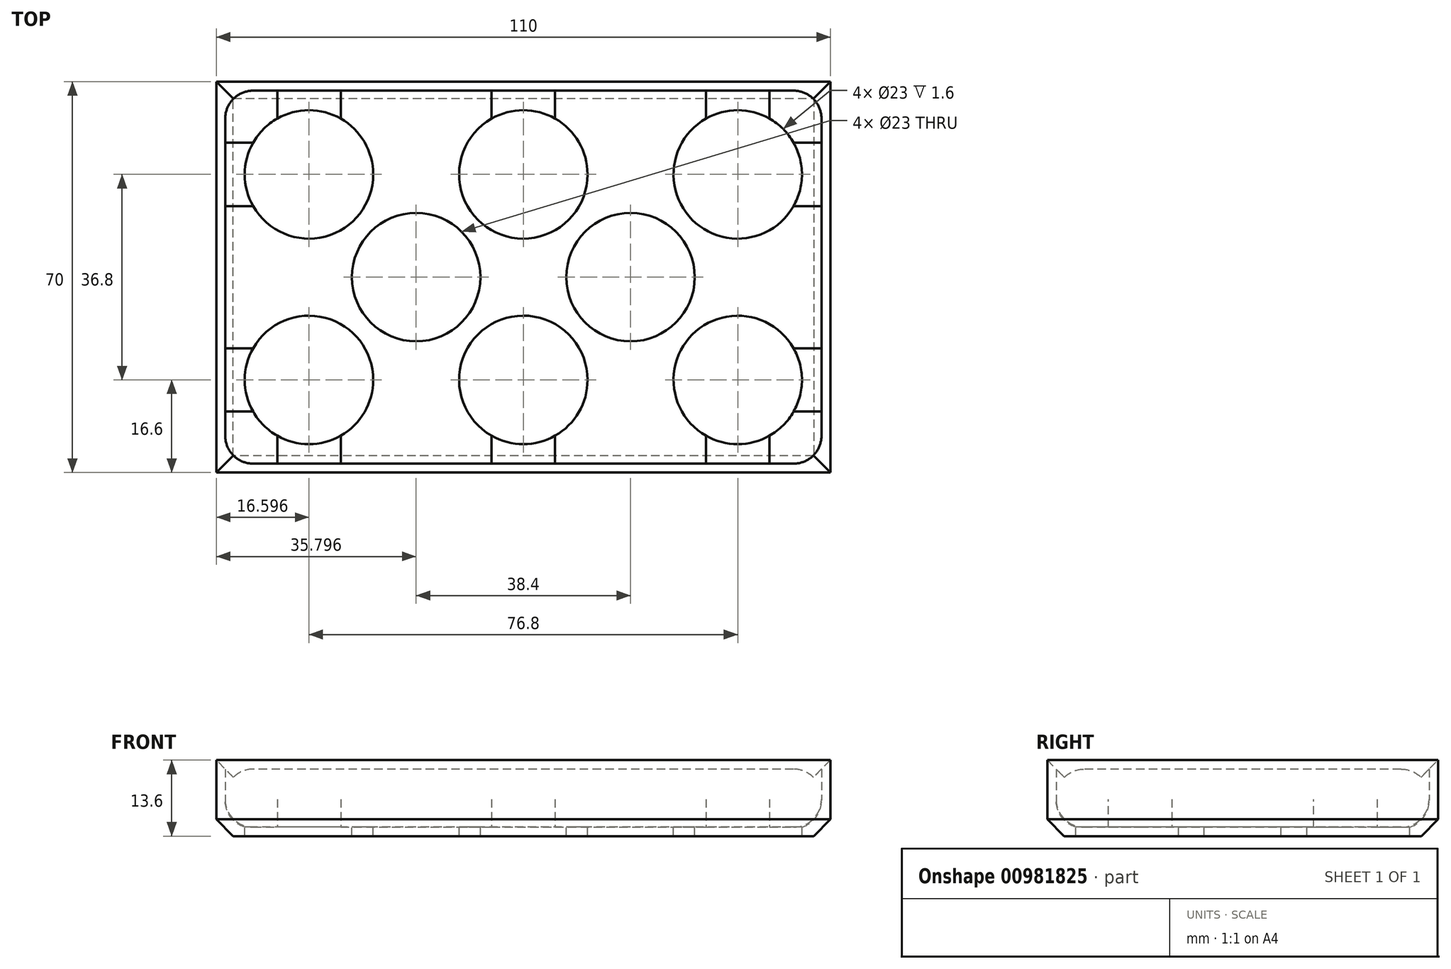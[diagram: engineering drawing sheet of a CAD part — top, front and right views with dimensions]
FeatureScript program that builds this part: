
annotation { "Feature Type Name" : "Feature", "Feature Type Description" : "" }
export const myFeature = defineFeature(function(context is Context, id is Id, definition is map)
    precondition{}
    {
        {
            var Q0;
            Q0=qCreatedBy(makeId("Top.planeOp"),FACE);
            var sketch = newSketch(context, id + "F0", { "sketchPlane" : qUnion([Q0])});
            skLineSegment(sketch, "E0.bottom", {"start": v(-42.8, 28.8) * mm, "end": v(67.2, 28.8) * mm});
            skLineSegment(sketch, "E0.top", {"start": v(-42.8, -41.2) * mm, "end": v(67.2, -41.2) * mm});
            skLineSegment(sketch, "E0.left", {"start": v(-42.8, 28.8) * mm, "end": v(-42.8, -41.2) * mm});
            skLineSegment(sketch, "E0.right", {"start": v(67.2, 28.8) * mm, "end": v(67.2, -41.2) * mm});
            skSolve(sketch);
        }
        {
            var Q0;
            Q0=makeQuery(id+"F0.imprint","IMPRINT",FACE,{"disambiguationData":[TD([[makeQuery(id+"F0.imprint","IMPRINT",EDGE,{"derivedFrom":sQuery(id+"F0.wireOp",EDGE,"E0.bottom")}),-1.0]])]});
            extrude(context, id + "F1", {"entities" : qUnion([Q0]), "depth" : 15 * mm, "offsetDistance" : 25 * mm});
        }
        {
            var Q0;
            Q0=makeQuery(id+"F1.opExtrude","CAP_FACE",FACE,{"disambiguationData":[OSD([sQuery(id+"F0.wireOp",EDGE,"E0.bottom"),sQuery(id+"F0.wireOp",EDGE,"E0.top"),sQuery(id+"F0.wireOp",EDGE,"E0.left"),sQuery(id+"F0.wireOp",EDGE,"E0.right")])],"isStart":false});
            shell(context, id + "F2", {"entities" : qUnion([Q0]), "thickness" : 1.6 * mm});
        }
        {
            var Q0;
            Q0=makeQuery(id+"F2.opShell","OFFSET_FACE",FACE,{"disambiguationData":[OSD([sQuery(id+"F0.wireOp",EDGE,"E0.bottom"),sQuery(id+"F0.wireOp",EDGE,"E0.top"),sQuery(id+"F0.wireOp",EDGE,"E0.left"),sQuery(id+"F0.wireOp",EDGE,"E0.right")])]});
            var sketch = newSketch(context, id + "F3", { "sketchPlane" : qUnion([Q0])});
            skCircle(sketch, "E1", {"center": v(50.6, 12.2) * mm, "radius": 11.5 * mm});
            skCircle(sketch, "E2.1.0.0", {"center": v(12.2, 12.2) * mm, "radius": 11.5 * mm});
            skCircle(sketch, "E2.2.0.0", {"center": v(-26.2, 12.2) * mm, "radius": 11.5 * mm});
            skLineSegment(sketch, "E2.direction1", {"start": v(50.6, 12.2) * mm, "end": v(12.2, 12.2) * mm, "construction": true});
            skCircle(sketch, "E3", {"center": v(50.6, -24.6) * mm, "radius": 11.5 * mm});
            skCircle(sketch, "E4.1.0.0", {"center": v(12.2, -24.6) * mm, "radius": 11.5 * mm});
            skCircle(sketch, "E4.2.0.0", {"center": v(-26.2, -24.6) * mm, "radius": 11.5 * mm});
            skLineSegment(sketch, "E4.direction1", {"start": v(50.6, -24.6) * mm, "end": v(12.2, -24.6) * mm, "construction": true});
            skCircle(sketch, "E5.2.0.0", {"center": v(-7, -6.2) * mm, "radius": 11.5 * mm});
            skCircle(sketch, "E6.1.0.0", {"center": v(31.4, -6.2) * mm, "radius": 11.5 * mm});
            skLineSegment(sketch, "E6.direction1", {"start": v(-7, -6.2) * mm, "end": v(31.4, -6.2) * mm, "construction": true});
            skSolve(sketch);
        }
        {
            var Q0;
            Q0=makeQuery(id+"F3.imprint","IMPRINT",FACE,{"disambiguationData":[TD([[makeQuery(id+"F3.imprint","IMPRINT",EDGE,{"derivedFrom":sQuery(id+"F3.wireOp",EDGE,"E2.3.0.0")}),1.0]])]});
            var Q1;
            Q1=makeQuery(id+"F3.imprint","IMPRINT",FACE,{"disambiguationData":[TD([[makeQuery(id+"F3.imprint","IMPRINT",EDGE,{"derivedFrom":sQuery(id+"F3.wireOp",EDGE,"E2.2.0.0")}),1.0]])]});
            var Q2;
            Q2=makeQuery(id+"F3.imprint","IMPRINT",FACE,{"disambiguationData":[TD([[makeQuery(id+"F3.imprint","IMPRINT",EDGE,{"derivedFrom":sQuery(id+"F3.wireOp",EDGE,"E2.1.0.0")}),1.0]])]});
            var Q3;
            Q3=makeQuery(id+"F3.imprint","IMPRINT",FACE,{"disambiguationData":[TD([[makeQuery(id+"F3.imprint","IMPRINT",EDGE,{"derivedFrom":sQuery(id+"F3.wireOp",EDGE,"E1")}),1.0]])]});
            var Q4;
            Q4=makeQuery(id+"F3.imprint","IMPRINT",FACE,{"disambiguationData":[TD([[makeQuery(id+"F3.imprint","IMPRINT",EDGE,{"derivedFrom":sQuery(id+"F3.wireOp",EDGE,"E6.2.0.0")}),1.0]])]});
            var Q5;
            Q5=makeQuery(id+"F3.imprint","IMPRINT",FACE,{"disambiguationData":[TD([[makeQuery(id+"F3.imprint","IMPRINT",EDGE,{"derivedFrom":sQuery(id+"F3.wireOp",EDGE,"E3")}),1.0]])]});
            var Q6;
            Q6=makeQuery(id+"F3.imprint","IMPRINT",FACE,{"disambiguationData":[TD([[makeQuery(id+"F3.imprint","IMPRINT",EDGE,{"derivedFrom":sQuery(id+"F3.wireOp",EDGE,"E4.1.0.0")}),1.0]])]});
            var Q7;
            Q7=makeQuery(id+"F3.imprint","IMPRINT",FACE,{"disambiguationData":[TD([[makeQuery(id+"F3.imprint","IMPRINT",EDGE,{"derivedFrom":sQuery(id+"F3.wireOp",EDGE,"E6.1.0.0")}),1.0]])]});
            var Q8;
            Q8=makeQuery(id+"F3.imprint","IMPRINT",FACE,{"disambiguationData":[TD([[makeQuery(id+"F3.imprint","IMPRINT",EDGE,{"derivedFrom":sQuery(id+"F3.wireOp",EDGE,"E4.2.0.0")}),1.0]])]});
            var Q9;
            Q9=makeQuery(id+"F3.imprint","IMPRINT",FACE,{"disambiguationData":[TD([[makeQuery(id+"F3.imprint","IMPRINT",EDGE,{"derivedFrom":sQuery(id+"F3.wireOp",EDGE,"E5.2.0.0")}),1.0]])]});
            var Q10;
            Q10=makeQuery(id+"F3.imprint","IMPRINT",FACE,{"disambiguationData":[TD([[makeQuery(id+"F3.imprint","IMPRINT",EDGE,{"derivedFrom":sQuery(id+"F3.wireOp",EDGE,"E4.3.0.0")}),1.0]])]});
            extrude(context, id + "F4", {"entities" : qUnion([Q0, Q1, Q2, Q3, Q4, Q5, Q6, Q7, Q8, Q9, Q10]), "operationType" : NewBodyOperationType.REMOVE, "oppositeDirection" : true, "depth" : 5 * mm, "offsetDistance" : 25 * mm});
        }
        {
            var Q0;
            Q0=makeQuery(id+"F1.opExtrude","CAP_EDGE",EDGE,{"disambiguationData":[OSD([sQuery(id+"F0.wireOp",EDGE,"E0.left")])],"isStart":true});
            var Q1;
            Q1=makeQuery(id+"F1.opExtrude","CAP_EDGE",EDGE,{"disambiguationData":[OSD([sQuery(id+"F0.wireOp",EDGE,"E0.top")])],"isStart":true});
            var Q2;
            Q2=makeQuery(id+"F1.opExtrude","CAP_EDGE",EDGE,{"disambiguationData":[OSD([sQuery(id+"F0.wireOp",EDGE,"E0.right")])],"isStart":true});
            var Q3;
            Q3=makeQuery(id+"F1.opExtrude","CAP_EDGE",EDGE,{"disambiguationData":[OSD([sQuery(id+"F0.wireOp",EDGE,"E0.bottom")])],"isStart":true});
            chamfer(context, id + "F5", {"entities" : qUnion([Q0, Q1, Q2, Q3]), "width" : 3 * mm, "tangentPropagation" : true});
        }
        {
            var Q0;
            {var subQ0=sQuery(id+"F0.wireOp",EDGE,"E0.bottom");Q0=makeQuery(id+"F2.opShell","OFFSET_EDGE",EDGE,{"disambiguationData":[OSD([subQ0]),TDD([makeQuery(id+"F1.opExtrude","CAP_EDGE",EDGE,{"disambiguationData":[OSD([subQ0])],"isStart":false})])]});}
            var Q1;
            {var subQ0=sQuery(id+"F0.wireOp",EDGE,"E0.left");Q1=makeQuery(id+"F2.opShell","OFFSET_EDGE",EDGE,{"disambiguationData":[OSD([subQ0]),TDD([makeQuery(id+"F1.opExtrude","CAP_EDGE",EDGE,{"disambiguationData":[OSD([subQ0])],"isStart":false})])]});}
            var Q2;
            {var subQ0=sQuery(id+"F0.wireOp",EDGE,"E0.right");Q2=makeQuery(id+"F2.opShell","OFFSET_EDGE",EDGE,{"disambiguationData":[OSD([subQ0]),TDD([makeQuery(id+"F1.opExtrude","CAP_EDGE",EDGE,{"disambiguationData":[OSD([subQ0])],"isStart":false})])]});}
            var Q3;
            {var subQ0=sQuery(id+"F0.wireOp",EDGE,"E0.top");Q3=makeQuery(id+"F2.opShell","OFFSET_EDGE",EDGE,{"disambiguationData":[OSD([subQ0]),TDD([makeQuery(id+"F1.opExtrude","CAP_EDGE",EDGE,{"disambiguationData":[OSD([subQ0])],"isStart":false})])]});}
            chamfer(context, id + "F6", {"entities" : qUnion([Q0, Q1, Q2, Q3]), "width" : 3 * mm, "tangentPropagation" : true});
        }
        {
            var Q0;
            {var subQ0=sQuery(id+"F0.wireOp",EDGE,"E0.left");Q0=makeQuery(id+"F2.opShell","OFFSET_EDGE",EDGE,{"disambiguationData":[OSD([subQ0]),TDD([makeQuery(id+"F1.opExtrude","CAP_EDGE",EDGE,{"disambiguationData":[OSD([subQ0])],"isStart":true})])]});}
            var Q1;
            {var subQ0=sQuery(id+"F0.wireOp",EDGE,"E0.right");Q1=makeQuery(id+"F2.opShell","OFFSET_EDGE",EDGE,{"disambiguationData":[OSD([subQ0]),TDD([makeQuery(id+"F1.opExtrude","CAP_EDGE",EDGE,{"disambiguationData":[OSD([subQ0])],"isStart":true})])]});}
            fillet(context, id + "F7", {"entities" : qUnion([Q0, Q1]), "radius" : 5 * mm, "tangentPropagation" : true, "allowEdgeOverflow" : false});
        }
        {
            var Q0;
            {var subQ0=sQuery(id+"F3.wireOp",EDGE,"E1");var subQ1=sQuery(id+"F0.wireOp",EDGE,"E0.bottom");var subQ2=makeQuery(id+"F2.opShell","OFFSET_FACE",FACE,{"disambiguationData":[OSD([subQ1,sQuery(id+"F0.wireOp",EDGE,"E0.top"),sQuery(id+"F0.wireOp",EDGE,"E0.left"),sQuery(id+"F0.wireOp",EDGE,"E0.right")])]});var subQ3=makeQuery(id+"F2.opShell","OFFSET_FACE",FACE,{"disambiguationData":[OSD([subQ1])]});var subQ4=sQuery(id+"F3.wireOp",EDGE,"E2.1.0.0");Q0=makeQuery(id+"F4.boolean.opBoolean","SPLIT",EDGE,{"disambiguationData":[topologyDisambiguationEdgeConnected([subQ3,subQ2]),TD([subQ3,subQ2,makeQuery(id+"F4.opExtrude","SWEPT_FACE",FACE,{"disambiguationData":[OSD([subQ0])]}),makeQuery(id+"F4.opExtrude","CAP_FACE",FACE,{"disambiguationData":[OSD([subQ0])],"isStart":true}),makeQuery(id+"F4.opExtrude","SWEPT_FACE",FACE,{"disambiguationData":[OSD([subQ4])]}),makeQuery(id+"F4.opExtrude","CAP_FACE",FACE,{"disambiguationData":[OSD([subQ4])],"isStart":true})])],"derivedFrom":makeQuery(id+"F2.opShell","OFFSET_EDGE",EDGE,{"disambiguationData":[OSD([subQ1]),TDD([makeQuery(id+"F1.opExtrude","CAP_EDGE",EDGE,{"disambiguationData":[OSD([subQ1])],"isStart":true})])]})});}
            var Q1;
            {var subQ0=sQuery(id+"F3.wireOp",EDGE,"E2.1.0.0");var subQ1=sQuery(id+"F0.wireOp",EDGE,"E0.bottom");var subQ2=makeQuery(id+"F2.opShell","OFFSET_FACE",FACE,{"disambiguationData":[OSD([subQ1,sQuery(id+"F0.wireOp",EDGE,"E0.top"),sQuery(id+"F0.wireOp",EDGE,"E0.left"),sQuery(id+"F0.wireOp",EDGE,"E0.right")])]});var subQ3=sQuery(id+"F3.wireOp",EDGE,"E2.2.0.0");var subQ4=makeQuery(id+"F2.opShell","OFFSET_FACE",FACE,{"disambiguationData":[OSD([subQ1])]});Q1=makeQuery(id+"F4.boolean.opBoolean","SPLIT",EDGE,{"disambiguationData":[topologyDisambiguationEdgeConnected([subQ4,subQ2]),TD([subQ4,subQ2,makeQuery(id+"F4.opExtrude","SWEPT_FACE",FACE,{"disambiguationData":[OSD([subQ0])]}),makeQuery(id+"F4.opExtrude","CAP_FACE",FACE,{"disambiguationData":[OSD([subQ0])],"isStart":true}),makeQuery(id+"F4.opExtrude","SWEPT_FACE",FACE,{"disambiguationData":[OSD([subQ3])]}),makeQuery(id+"F4.opExtrude","CAP_FACE",FACE,{"disambiguationData":[OSD([subQ3])],"isStart":true})])],"derivedFrom":makeQuery(id+"F2.opShell","OFFSET_EDGE",EDGE,{"disambiguationData":[OSD([subQ1]),TDD([makeQuery(id+"F1.opExtrude","CAP_EDGE",EDGE,{"disambiguationData":[OSD([subQ1])],"isStart":true})])]})});}
            var Q2;
            {var subQ0=sQuery(id+"F3.wireOp",EDGE,"E2.2.0.0");var subQ1=sQuery(id+"F0.wireOp",EDGE,"E0.bottom");var subQ2=makeQuery(id+"F2.opShell","OFFSET_FACE",FACE,{"disambiguationData":[OSD([subQ1,sQuery(id+"F0.wireOp",EDGE,"E0.top"),sQuery(id+"F0.wireOp",EDGE,"E0.left"),sQuery(id+"F0.wireOp",EDGE,"E0.right")])]});var subQ3=makeQuery(id+"F2.opShell","OFFSET_FACE",FACE,{"disambiguationData":[OSD([subQ1])]});var subQ4=sQuery(id+"F3.wireOp",EDGE,"E2.3.0.0");Q2=makeQuery(id+"F4.boolean.opBoolean","SPLIT",EDGE,{"disambiguationData":[topologyDisambiguationEdgeConnected([subQ3,subQ2]),TD([subQ3,subQ2,makeQuery(id+"F4.opExtrude","SWEPT_FACE",FACE,{"disambiguationData":[OSD([subQ0])]}),makeQuery(id+"F4.opExtrude","CAP_FACE",FACE,{"disambiguationData":[OSD([subQ0])],"isStart":true}),makeQuery(id+"F4.opExtrude","SWEPT_FACE",FACE,{"disambiguationData":[OSD([subQ4])]}),makeQuery(id+"F4.opExtrude","CAP_FACE",FACE,{"disambiguationData":[OSD([subQ4])],"isStart":true})])],"derivedFrom":makeQuery(id+"F2.opShell","OFFSET_EDGE",EDGE,{"disambiguationData":[OSD([subQ1]),TDD([makeQuery(id+"F1.opExtrude","CAP_EDGE",EDGE,{"disambiguationData":[OSD([subQ1])],"isStart":true})])]})});}
            var Q3;
            {var subQ0=sQuery(id+"F3.wireOp",EDGE,"E3");var subQ1=sQuery(id+"F0.wireOp",EDGE,"E0.top");var subQ2=makeQuery(id+"F2.opShell","OFFSET_FACE",FACE,{"disambiguationData":[OSD([subQ1])]});var subQ3=makeQuery(id+"F2.opShell","OFFSET_FACE",FACE,{"disambiguationData":[OSD([sQuery(id+"F0.wireOp",EDGE,"E0.bottom"),subQ1,sQuery(id+"F0.wireOp",EDGE,"E0.left"),sQuery(id+"F0.wireOp",EDGE,"E0.right")])]});var subQ4=sQuery(id+"F3.wireOp",EDGE,"E4.1.0.0");Q3=makeQuery(id+"F4.boolean.opBoolean","SPLIT",EDGE,{"disambiguationData":[topologyDisambiguationEdgeConnected([subQ3,subQ2]),TD([subQ3,subQ2,makeQuery(id+"F4.opExtrude","SWEPT_FACE",FACE,{"disambiguationData":[OSD([subQ0])]}),makeQuery(id+"F4.opExtrude","CAP_FACE",FACE,{"disambiguationData":[OSD([subQ0])],"isStart":true}),makeQuery(id+"F4.opExtrude","SWEPT_FACE",FACE,{"disambiguationData":[OSD([subQ4])]}),makeQuery(id+"F4.opExtrude","CAP_FACE",FACE,{"disambiguationData":[OSD([subQ4])],"isStart":true})])],"derivedFrom":makeQuery(id+"F2.opShell","OFFSET_EDGE",EDGE,{"disambiguationData":[OSD([subQ1]),TDD([makeQuery(id+"F1.opExtrude","CAP_EDGE",EDGE,{"disambiguationData":[OSD([subQ1])],"isStart":true})])]})});}
            var Q4;
            {var subQ0=sQuery(id+"F3.wireOp",EDGE,"E4.1.0.0");var subQ1=sQuery(id+"F0.wireOp",EDGE,"E0.top");var subQ2=makeQuery(id+"F2.opShell","OFFSET_FACE",FACE,{"disambiguationData":[OSD([subQ1])]});var subQ3=sQuery(id+"F3.wireOp",EDGE,"E4.2.0.0");var subQ4=makeQuery(id+"F2.opShell","OFFSET_FACE",FACE,{"disambiguationData":[OSD([sQuery(id+"F0.wireOp",EDGE,"E0.bottom"),subQ1,sQuery(id+"F0.wireOp",EDGE,"E0.left"),sQuery(id+"F0.wireOp",EDGE,"E0.right")])]});Q4=makeQuery(id+"F4.boolean.opBoolean","SPLIT",EDGE,{"disambiguationData":[topologyDisambiguationEdgeConnected([subQ4,subQ2]),TD([subQ4,subQ2,makeQuery(id+"F4.opExtrude","SWEPT_FACE",FACE,{"disambiguationData":[OSD([subQ0])]}),makeQuery(id+"F4.opExtrude","CAP_FACE",FACE,{"disambiguationData":[OSD([subQ0])],"isStart":true}),makeQuery(id+"F4.opExtrude","SWEPT_FACE",FACE,{"disambiguationData":[OSD([subQ3])]}),makeQuery(id+"F4.opExtrude","CAP_FACE",FACE,{"disambiguationData":[OSD([subQ3])],"isStart":true})])],"derivedFrom":makeQuery(id+"F2.opShell","OFFSET_EDGE",EDGE,{"disambiguationData":[OSD([subQ1]),TDD([makeQuery(id+"F1.opExtrude","CAP_EDGE",EDGE,{"disambiguationData":[OSD([subQ1])],"isStart":true})])]})});}
            var Q5;
            {var subQ0=sQuery(id+"F3.wireOp",EDGE,"E4.2.0.0");var subQ1=sQuery(id+"F0.wireOp",EDGE,"E0.top");var subQ2=makeQuery(id+"F2.opShell","OFFSET_FACE",FACE,{"disambiguationData":[OSD([subQ1])]});var subQ3=makeQuery(id+"F2.opShell","OFFSET_FACE",FACE,{"disambiguationData":[OSD([sQuery(id+"F0.wireOp",EDGE,"E0.bottom"),subQ1,sQuery(id+"F0.wireOp",EDGE,"E0.left"),sQuery(id+"F0.wireOp",EDGE,"E0.right")])]});var subQ4=sQuery(id+"F3.wireOp",EDGE,"E4.3.0.0");Q5=makeQuery(id+"F4.boolean.opBoolean","SPLIT",EDGE,{"disambiguationData":[topologyDisambiguationEdgeConnected([subQ3,subQ2]),TD([subQ3,subQ2,makeQuery(id+"F4.opExtrude","SWEPT_FACE",FACE,{"disambiguationData":[OSD([subQ0])]}),makeQuery(id+"F4.opExtrude","CAP_FACE",FACE,{"disambiguationData":[OSD([subQ0])],"isStart":true}),makeQuery(id+"F4.opExtrude","SWEPT_FACE",FACE,{"disambiguationData":[OSD([subQ4])]}),makeQuery(id+"F4.opExtrude","CAP_FACE",FACE,{"disambiguationData":[OSD([subQ4])],"isStart":true})])],"derivedFrom":makeQuery(id+"F2.opShell","OFFSET_EDGE",EDGE,{"disambiguationData":[OSD([subQ1]),TDD([makeQuery(id+"F1.opExtrude","CAP_EDGE",EDGE,{"disambiguationData":[OSD([subQ1])],"isStart":true})])]})});}
            fillet(context, id + "F8", {"entities" : qUnion([Q0, Q1, Q2, Q3, Q4, Q5]), "radius" : 5 * mm, "tangentPropagation" : true, "allowEdgeOverflow" : false});
        }
    });
